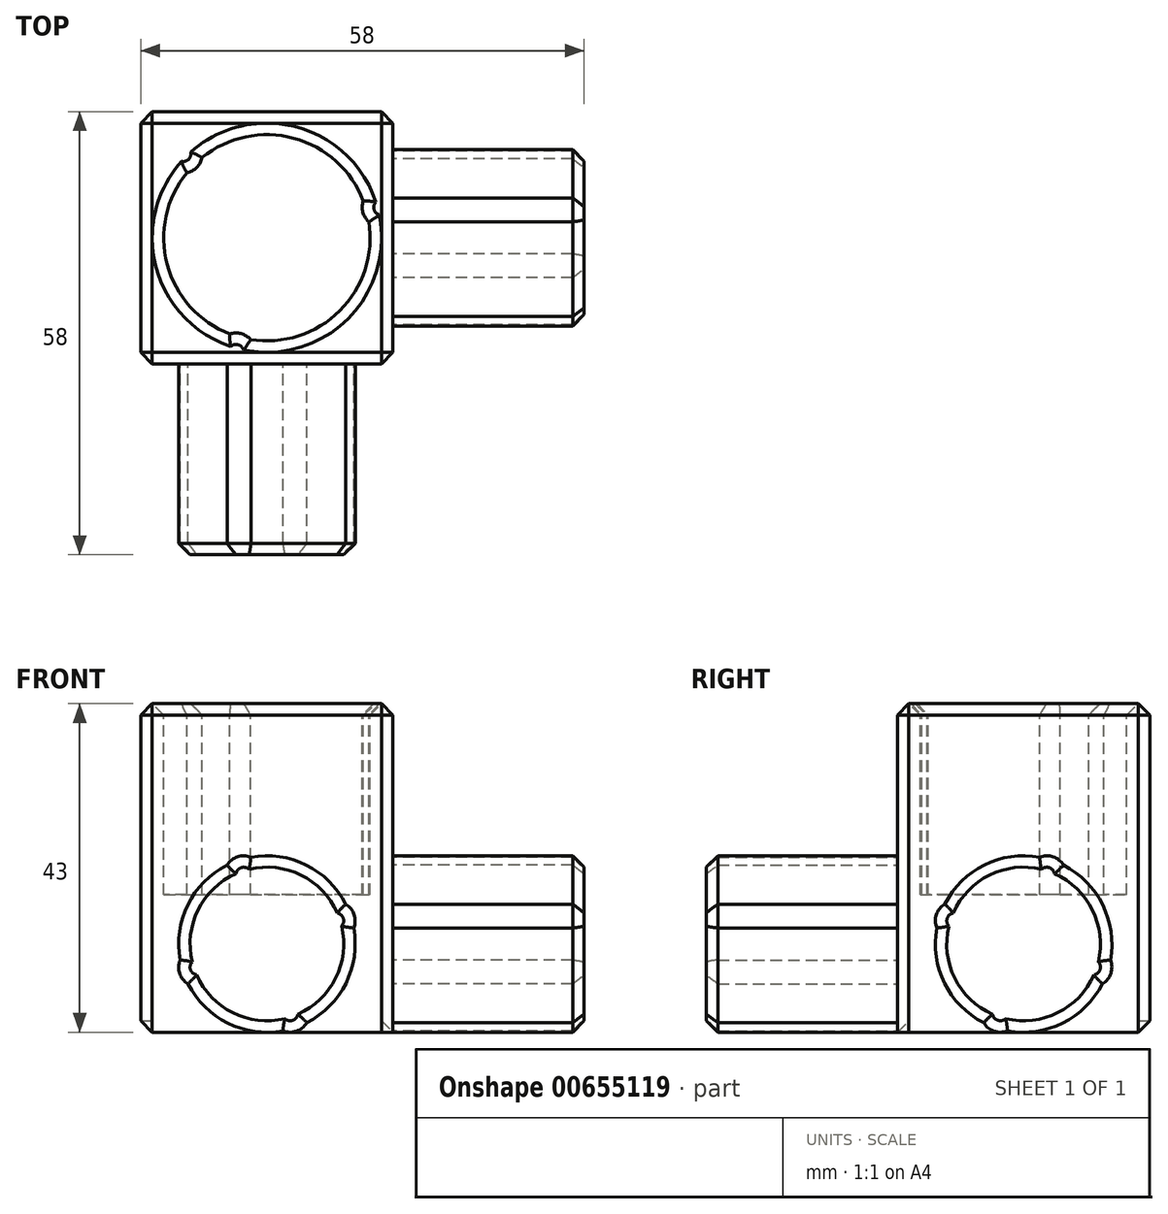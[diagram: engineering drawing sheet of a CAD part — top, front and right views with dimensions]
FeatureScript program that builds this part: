
annotation { "Feature Type Name" : "Feature", "Feature Type Description" : "" }
export const myFeature = defineFeature(function(context is Context, id is Id, definition is map)
    precondition{}
    {
        {
            var Q0;
            Q0=qCreatedBy(makeId("Front.planeOp"),FACE);
            var sketch = newSketch(context, id + "F0", { "sketchPlane" : qUnion([Q0])});
            skLineSegment(sketch, "E0.bottom", {"start": v(-16.5, 0) * mm, "end": v(16.5, 0) * mm});
            skLineSegment(sketch, "E0.top", {"start": v(-16.5, 43) * mm, "end": v(16.5, 43) * mm});
            skLineSegment(sketch, "E0.left", {"start": v(-16.5, 0) * mm, "end": v(-16.5, 43) * mm});
            skLineSegment(sketch, "E0.right", {"start": v(16.5, 0) * mm, "end": v(16.5, 43) * mm});
            skSolve(sketch);
        }
        {
            var Q0;
            Q0=qSketchRegion(id+"F0",true);
            var Q1;
            Q1 = qSketchRegion(id + "F2", true);
            extrude(context, id + "F1", {"entities" : qUnion([Q0, Q1]), "depth" : 33 * mm, "offsetDistance" : 25 * mm, "symmetric" : true});
        }
        {
            var Q0;
            Q0=makeQuery(id+"F1.opExtrude","CAP_FACE",FACE,{"disambiguationData":[OSD([sQuery(id+"F0.wireOp",EDGE,"E0.bottom"),sQuery(id+"F0.wireOp",EDGE,"E0.top"),sQuery(id+"F0.wireOp",EDGE,"E0.left"),sQuery(id+"F0.wireOp",EDGE,"E0.right")])],"isStart":false});
            var sketch = newSketch(context, id + "F2", { "sketchPlane" : qUnion([Q0])});
            skArc(sketch, "E1", {"start": v(-10.3, 6.34) * mm, "mid": v(-5.13, 1.2) * mm, "end": v(2.1, 0.2) * mm});
            skArc(sketch, "E2", {"start": v(-11.36, 9.46) * mm, "mid": v(-11.42, 7.7) * mm, "end": v(-10.3, 6.34) * mm});
            skArc(sketch, "E3.1.0", {"start": v(2.1, 0.2) * mm, "mid": v(3.85, 0.13) * mm, "end": v(5.2, 1.24) * mm});
            skArc(sketch, "E3.2.0", {"start": v(11.36, 13.64) * mm, "mid": v(11.42, 15.4) * mm, "end": v(10.3, 16.76) * mm});
            skArc(sketch, "E4.1.3.0", {"start": v(-2.1, 22.9) * mm, "mid": v(-3.85, 22.97) * mm, "end": v(-5.2, 21.86) * mm});
            skArc(sketch, "E5.trimOffspring", {"start": v(-5.2, 21.86) * mm, "mid": v(-10.35, 16.68) * mm, "end": v(-11.36, 9.46) * mm});
            skArc(sketch, "E6.trimOffspring", {"start": v(10.3, 16.76) * mm, "mid": v(5.13, 21.9) * mm, "end": v(-2.1, 22.9) * mm});
            skArc(sketch, "E7.trimOffspring", {"start": v(5.2, 1.24) * mm, "mid": v(10.35, 6.42) * mm, "end": v(11.36, 13.64) * mm});
            skSolve(sketch);
        }
        {
            var Q0;
            Q0=makeQuery(id+"F2.imprint","IMPRINT",FACE,{"disambiguationData":[TD([[makeQuery(id+"F2.imprint","IMPRINT",EDGE,{"derivedFrom":sQuery(id+"F2.wireOp",EDGE,"E1")}),1.0]])]});
            extrude(context, id + "F3", {"entities" : qUnion([Q0]), "operationType" : NewBodyOperationType.ADD, "depth" : 25 * mm, "offsetDistance" : 25 * mm});
        }
        {
            var Q0;
            Q0=makeQuery(id+"F1.opExtrude","SWEPT_FACE",FACE,{"disambiguationData":[OSD([sQuery(id+"F0.wireOp",EDGE,"E0.right")])]});
            var sketch = newSketch(context, id + "F4", { "sketchPlane" : qUnion([Q0])});
            skArc(sketch, "E8", {"start": v(-11.36, 13.64) * mm, "mid": v(-10.35, 6.42) * mm, "end": v(-5.2, 1.24) * mm});
            skArc(sketch, "E9", {"start": v(-10.3, 16.76) * mm, "mid": v(-11.42, 15.4) * mm, "end": v(-11.36, 13.64) * mm});
            skArc(sketch, "E10.1.0", {"start": v(-5.2, 1.24) * mm, "mid": v(-3.85, 0.13) * mm, "end": v(-2.1, 0.2) * mm});
            skArc(sketch, "E10.2.0", {"start": v(10.3, 6.34) * mm, "mid": v(11.42, 7.7) * mm, "end": v(11.36, 9.46) * mm});
            skArc(sketch, "E10.3.0", {"start": v(5.2, 21.86) * mm, "mid": v(3.85, 22.97) * mm, "end": v(2.1, 22.9) * mm});
            skArc(sketch, "E11.trimOffspring", {"start": v(2.1, 22.9) * mm, "mid": v(-5.13, 21.9) * mm, "end": v(-10.3, 16.76) * mm});
            skArc(sketch, "E12.trimOffspring", {"start": v(11.36, 9.46) * mm, "mid": v(10.35, 16.68) * mm, "end": v(5.2, 21.86) * mm});
            skArc(sketch, "E13.trimOffspring", {"start": v(-2.1, 0.2) * mm, "mid": v(5.13, 1.2) * mm, "end": v(10.3, 6.34) * mm});
            skSolve(sketch);
        }
        {
            var Q0;
            Q0=qSketchRegion(id+"F4",true);
            extrude(context, id + "F5", {"entities" : qUnion([Q0]), "operationType" : NewBodyOperationType.ADD, "depth" : 25 * mm, "offsetDistance" : 25 * mm});
        }
        {
            var Q0;
            Q0=makeQuery(id+"F1.opExtrude","SWEPT_FACE",FACE,{"disambiguationData":[OSD([sQuery(id+"F0.wireOp",EDGE,"E0.top")])]});
            var sketch = newSketch(context, id + "F6", { "sketchPlane" : qUnion([Q0])});
            skCircle(sketch, "E14", {"center": v(0, 0) * mm, "radius": 13.5 * mm});
            skCircle(sketch, "E15", {"center": v(-10.94, 10.98) * mm, "radius": 2.5 * mm});
            skCircle(sketch, "E16.1.0", {"center": v(-4.04, -14.96) * mm, "radius": 2.5 * mm});
            skCircle(sketch, "E16.2.0", {"center": v(14.98, 3.98) * mm, "radius": 2.5 * mm});
            skSolve(sketch);
        }
        {
            var Q0;
            Q0=makeQuery(id+"F6.imprint","IMPRINT",FACE,{"disambiguationData":[TD([[makeQuery(id+"F6.imprint","IMPRINT",EDGE,{"derivedFrom":sQuery(id+"F6.wireOp",EDGE,"E14")}),1.0]])]});
            extrude(context, id + "F7", {"entities" : qUnion([Q0]), "operationType" : NewBodyOperationType.REMOVE, "oppositeDirection" : true, "depth" : 25 * mm, "offsetDistance" : 25 * mm});
        }
        {
            var Q0;
            Q0=makeQuery(id+"F1.opExtrude","SWEPT_FACE",FACE,{"disambiguationData":[OSD([sQuery(id+"F0.wireOp",EDGE,"E0.top")])]});
            var Q1;
            Q1=makeQuery(id+"F1.opExtrude","CAP_FACE",FACE,{"disambiguationData":[OSD([sQuery(id+"F0.wireOp",EDGE,"E0.bottom"),sQuery(id+"F0.wireOp",EDGE,"E0.top"),sQuery(id+"F0.wireOp",EDGE,"E0.left"),sQuery(id+"F0.wireOp",EDGE,"E0.right")])],"isStart":true});
            var Q2;
            Q2=makeQuery(id+"F1.opExtrude","SWEPT_FACE",FACE,{"disambiguationData":[OSD([sQuery(id+"F0.wireOp",EDGE,"E0.left")])]});
            var Q3;
            Q3=makeQuery(id+"F1.opExtrude","CAP_EDGE",EDGE,{"disambiguationData":[OSD([sQuery(id+"F0.wireOp",EDGE,"E0.right")])],"isStart":false});
            var Q4;
            Q4=makeQuery(id+"F3.opExtrude","CAP_FACE",FACE,{"disambiguationData":[OSD([sQuery(id+"F2.wireOp",EDGE,"E1"),sQuery(id+"F2.wireOp",EDGE,"E2"),sQuery(id+"F2.wireOp",EDGE,"E3.1.0"),sQuery(id+"F2.wireOp",EDGE,"E3.2.0"),sQuery(id+"F2.wireOp",EDGE,"E4.1.3.0"),sQuery(id+"F2.wireOp",EDGE,"E5.trimOffspring"),sQuery(id+"F2.wireOp",EDGE,"E6.trimOffspring"),sQuery(id+"F2.wireOp",EDGE,"E7.trimOffspring")])],"isStart":false});
            var Q5;
            Q5=makeQuery(id+"F5.opExtrude","CAP_FACE",FACE,{"disambiguationData":[OSD([sQuery(id+"F4.wireOp",EDGE,"E8"),sQuery(id+"F4.wireOp",EDGE,"E9"),sQuery(id+"F4.wireOp",EDGE,"E10.1.0"),sQuery(id+"F4.wireOp",EDGE,"E10.2.0"),sQuery(id+"F4.wireOp",EDGE,"E10.3.0"),sQuery(id+"F4.wireOp",EDGE,"E11.trimOffspring"),sQuery(id+"F4.wireOp",EDGE,"E12.trimOffspring"),sQuery(id+"F4.wireOp",EDGE,"E13.trimOffspring")])],"isStart":false});
            chamfer(context, id + "F8", {"entities" : qUnion([Q0, Q1, Q2, Q3, Q4, Q5]), "width" : 1.5 * mm, "tangentPropagation" : true});
        }
    });
